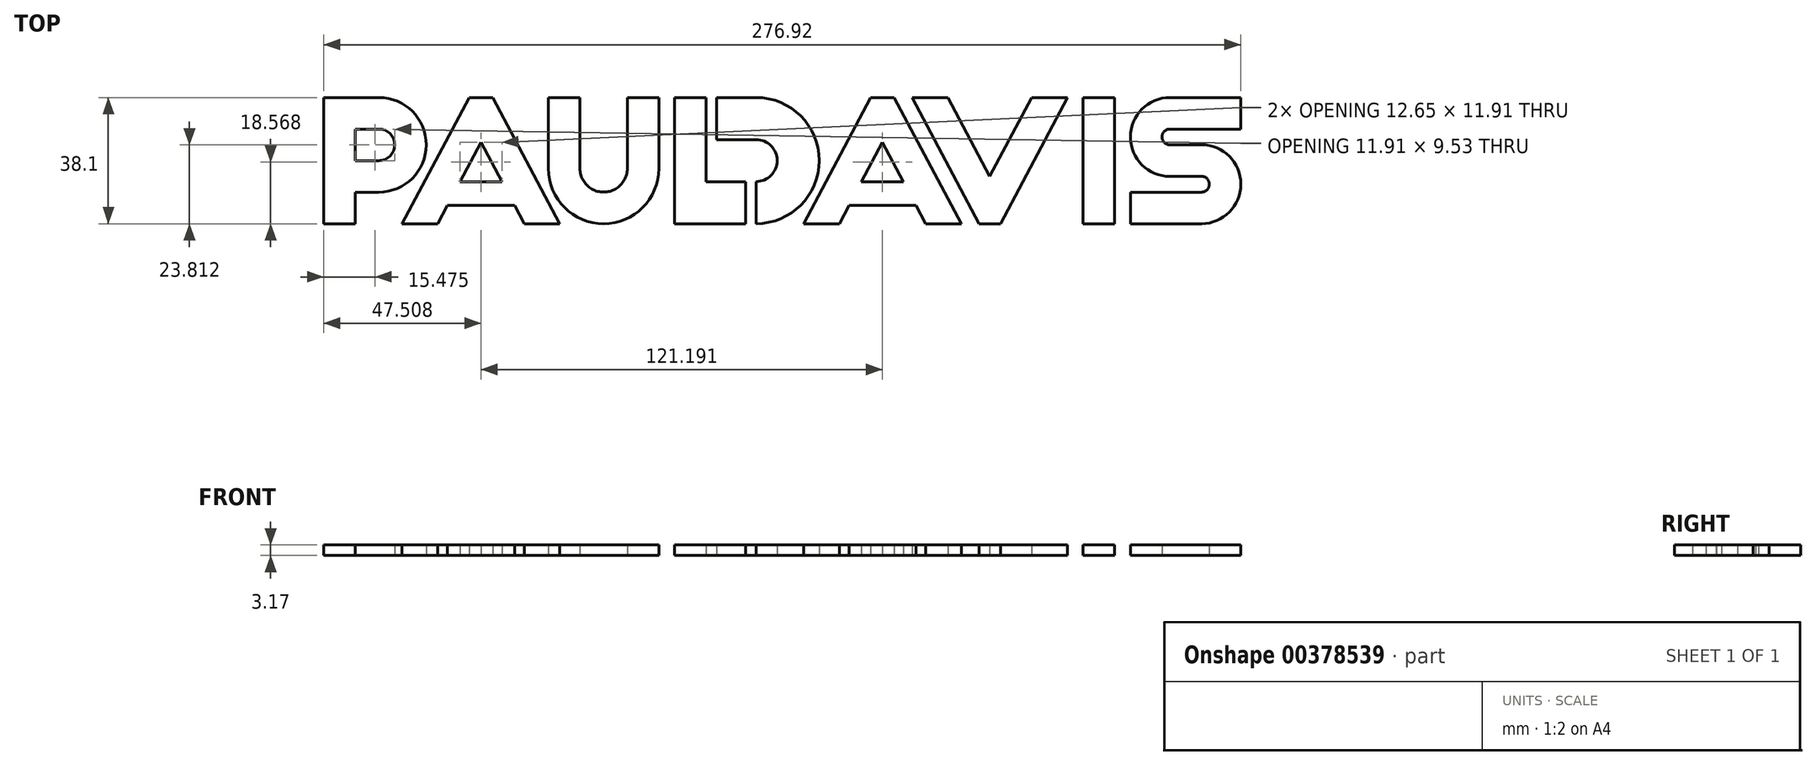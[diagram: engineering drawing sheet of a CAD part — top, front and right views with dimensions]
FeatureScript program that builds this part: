
annotation { "Feature Type Name" : "Feature", "Feature Type Description" : "" }
export const myFeature = defineFeature(function(context is Context, id is Id, definition is map)
    precondition{}
    {
        {
            var Q0;
            Q0=qCreatedBy(makeId("Top.planeOp"),FACE);
            var sketch = newSketch(context, id + "F0", { "sketchPlane" : qUnion([Q0])});
            skLineSegment(sketch, "E0.bottom", {"start": v(-32.5, 19.05) * mm, "end": v(-22.98, 19.05) * mm});
            skLineSegment(sketch, "E0.top", {"start": v(-32.5, -19.05) * mm, "end": v(-22.98, -19.05) * mm});
            skLineSegment(sketch, "E0.left", {"start": v(-32.5, 19.05) * mm, "end": v(-32.5, -19.05) * mm});
            skLineSegment(sketch, "E0.right", {"start": v(-22.98, 19.05) * mm, "end": v(-22.98, -6.35) * mm});
            skArc(sketch, "E1", {"start": v(-7.9, -19.05) * mm, "mid": v(11.15, 0) * mm, "end": v(-7.9, 19.05) * mm});
            skArc(sketch, "E2", {"start": v(-7.9, -6.35) * mm, "mid": v(-1.55, 0) * mm, "end": v(-7.9, 6.35) * mm});
            skLineSegment(sketch, "E3", {"start": v(-19.8, 19.05) * mm, "end": v(-7.9, 19.05) * mm});
            skLineSegment(sketch, "E4", {"start": v(-11.07, -19.05) * mm, "end": v(-22.98, -19.05) * mm});
            skLineSegment(sketch, "E5", {"start": v(-11.07, -6.35) * mm, "end": v(-22.98, -6.35) * mm});
            skLineSegment(sketch, "E6", {"start": v(-7.9, 6.35) * mm, "end": v(-19.8, 6.35) * mm});
            skLineSegment(sketch, "E7", {"start": v(-7.9, 19.05) * mm, "end": v(-7.9, -19.05) * mm, "construction": true});
            skLineSegment(sketch, "E8", {"start": v(-7.9, 0) * mm, "end": v(11.15, 0) * mm, "construction": true});
            skLineSegment(sketch, "E9", {"start": v(-19.8, 19.05) * mm, "end": v(-19.8, 6.35) * mm});
            skLineSegment(sketch, "E10", {"start": v(-7.9, 0) * mm, "end": v(-22.98, 0) * mm, "construction": true});
            skLineSegment(sketch, "E11", {"start": v(-11.07, -6.35) * mm, "end": v(-11.07, -19.05) * mm});
            skLineSegment(sketch, "E12", {"start": v(-7.9, -6.35) * mm, "end": v(-7.9, -19.05) * mm});
            skLineSegment(sketch, "E13", {"start": v(-32.5, -19.05) * mm, "end": v(11.15, -19.05) * mm, "construction": true});
            skLineSegment(sketch, "E14", {"start": v(11.15, -19.05) * mm, "end": v(11.15, 0) * mm, "construction": true});
            skLineSegment(sketch, "E15", {"start": v(-94.52, 19.05) * mm, "end": v(-87.38, 19.05) * mm});
            skLineSegment(sketch, "E16", {"start": v(-87.38, 19.05) * mm, "end": v(-67.14, -19.05) * mm});
            skLineSegment(sketch, "E17", {"start": v(-94.52, 19.05) * mm, "end": v(-114.76, -19.05) * mm});
            skArc(sketch, "E18", {"start": v(-70.6, -2.38) * mm, "mid": v(-53.93, -19.05) * mm, "end": v(-37.26, -2.38) * mm});
            skArc(sketch, "E19", {"start": v(-61.08, -2.38) * mm, "mid": v(-53.93, -9.52) * mm, "end": v(-46.79, -2.38) * mm});
            skLineSegment(sketch, "E20", {"start": v(-53.93, -19.05) * mm, "end": v(-53.93, -9.52) * mm, "construction": true});
            skLineSegment(sketch, "E21", {"start": v(-70.6, -2.38) * mm, "end": v(-61.08, -2.38) * mm, "construction": true});
            skLineSegment(sketch, "E22.trimOffspring", {"start": v(-46.79, -2.38) * mm, "end": v(-37.26, -2.38) * mm, "construction": true});
            skLineSegment(sketch, "E23", {"start": v(-70.6, -2.38) * mm, "end": v(-70.6, 19.05) * mm});
            skLineSegment(sketch, "E24", {"start": v(-70.6, 19.05) * mm, "end": v(-61.08, 19.05) * mm});
            skLineSegment(sketch, "E25", {"start": v(-61.08, 19.05) * mm, "end": v(-61.08, -2.38) * mm});
            skLineSegment(sketch, "E26", {"start": v(-46.79, -2.38) * mm, "end": v(-46.79, 19.05) * mm});
            skLineSegment(sketch, "E27", {"start": v(-46.79, 19.05) * mm, "end": v(-37.26, 19.05) * mm});
            skLineSegment(sketch, "E28", {"start": v(-37.26, 19.05) * mm, "end": v(-37.26, -2.38) * mm});
            skLineSegment(sketch, "E29", {"start": v(-37.26, -2.38) * mm, "end": v(-32.5, -2.38) * mm, "construction": true});
            skLineSegment(sketch, "E30", {"start": v(-101.07, -13.58) * mm, "end": v(-80.83, -13.58) * mm});
            skLineSegment(sketch, "E31", {"start": v(-97.28, -6.44) * mm, "end": v(-84.63, -6.44) * mm});
            skLineSegment(sketch, "E32", {"start": v(-90.95, 5.47) * mm, "end": v(-97.28, -6.44) * mm});
            skLineSegment(sketch, "E33", {"start": v(-77.93, -19.05) * mm, "end": v(-80.83, -13.58) * mm});
            skLineSegment(sketch, "E34", {"start": v(-114.76, -19.05) * mm, "end": v(-103.98, -19.05) * mm});
            skLineSegment(sketch, "E35", {"start": v(-67.14, -19.05) * mm, "end": v(-77.93, -19.05) * mm});
            skLineSegment(sketch, "E36", {"start": v(-114.76, -19.05) * mm, "end": v(-67.14, -19.05) * mm, "construction": true});
            skLineSegment(sketch, "E37.trimOffspring", {"start": v(-84.63, -6.44) * mm, "end": v(-90.95, 5.47) * mm});
            skLineSegment(sketch, "E38.trimOffspring", {"start": v(-101.07, -13.58) * mm, "end": v(-103.98, -19.05) * mm});
            skLineSegment(sketch, "E39", {"start": v(-70.6, -2.38) * mm, "end": v(-74.8, -4.62) * mm, "construction": true});
            skLineSegment(sketch, "E40", {"start": v(26.67, 19.05) * mm, "end": v(33.81, 19.05) * mm});
            skLineSegment(sketch, "E41", {"start": v(33.81, 19.05) * mm, "end": v(54.05, -19.05) * mm});
            skLineSegment(sketch, "E42", {"start": v(26.67, 19.05) * mm, "end": v(6.43, -19.05) * mm});
            skLineSegment(sketch, "E43", {"start": v(20.12, -13.58) * mm, "end": v(40.36, -13.58) * mm});
            skLineSegment(sketch, "E44", {"start": v(23.91, -6.44) * mm, "end": v(36.56, -6.44) * mm});
            skLineSegment(sketch, "E45", {"start": v(30.24, 5.47) * mm, "end": v(23.91, -6.44) * mm});
            skLineSegment(sketch, "E46", {"start": v(43.27, -19.05) * mm, "end": v(40.36, -13.58) * mm});
            skLineSegment(sketch, "E47", {"start": v(6.43, -19.05) * mm, "end": v(17.21, -19.05) * mm});
            skLineSegment(sketch, "E48", {"start": v(54.05, -19.05) * mm, "end": v(43.27, -19.05) * mm});
            skLineSegment(sketch, "E49", {"start": v(6.43, -19.05) * mm, "end": v(54.05, -19.05) * mm, "construction": true});
            skLineSegment(sketch, "E50.trimOffspring", {"start": v(36.56, -6.44) * mm, "end": v(30.24, 5.47) * mm});
            skLineSegment(sketch, "E51.trimOffspring", {"start": v(20.12, -13.58) * mm, "end": v(17.21, -19.05) * mm});
            skLineSegment(sketch, "E52", {"start": v(11.15, 0) * mm, "end": v(15.36, -2.23) * mm, "construction": true});
            skArc(sketch, "E53", {"start": v(-121.8, -9.53) * mm, "mid": v(-107.5, 4.76) * mm, "end": v(-121.8, 19.05) * mm});
            skArc(sketch, "E54", {"start": v(-121.8, 0) * mm, "mid": v(-117.03, 4.76) * mm, "end": v(-121.8, 9.52) * mm});
            skLineSegment(sketch, "E55", {"start": v(-121.8, 19.05) * mm, "end": v(-94.52, 19.05) * mm, "construction": true});
            skLineSegment(sketch, "E56", {"start": v(-107.5, 4.76) * mm, "end": v(-103.3, 2.53) * mm, "construction": true});
            skLineSegment(sketch, "E57", {"start": v(-121.8, 19.05) * mm, "end": v(-138.46, 19.05) * mm});
            skLineSegment(sketch, "E58", {"start": v(-121.8, 9.52) * mm, "end": v(-128.94, 9.52) * mm});
            skLineSegment(sketch, "E59", {"start": v(-121.8, 0) * mm, "end": v(-128.94, 0) * mm});
            skLineSegment(sketch, "E60", {"start": v(-121.8, -9.53) * mm, "end": v(-128.94, -9.53) * mm});
            skLineSegment(sketch, "E61", {"start": v(-138.46, 19.05) * mm, "end": v(-138.46, -19.05) * mm});
            skLineSegment(sketch, "E62", {"start": v(-138.46, -19.05) * mm, "end": v(-128.94, -19.05) * mm});
            skLineSegment(sketch, "E63", {"start": v(-128.94, -19.05) * mm, "end": v(-128.94, -9.53) * mm});
            skLineSegment(sketch, "E64", {"start": v(-128.94, 9.52) * mm, "end": v(-128.94, 0) * mm});
            skLineSegment(sketch, "E65", {"start": v(39.2, 19.05) * mm, "end": v(49.99, 19.05) * mm});
            skLineSegment(sketch, "E66", {"start": v(49.99, 19.05) * mm, "end": v(62.64, -4.76) * mm});
            skLineSegment(sketch, "E67", {"start": v(62.64, -4.76) * mm, "end": v(75.3, 19.05) * mm});
            skLineSegment(sketch, "E68", {"start": v(75.3, 19.05) * mm, "end": v(86.08, 19.05) * mm});
            skLineSegment(sketch, "E69", {"start": v(86.08, 19.05) * mm, "end": v(65.84, -19.05) * mm});
            skLineSegment(sketch, "E70", {"start": v(65.84, -19.05) * mm, "end": v(59.44, -19.05) * mm});
            skLineSegment(sketch, "E71", {"start": v(59.44, -19.05) * mm, "end": v(39.2, 19.05) * mm});
            skLineSegment(sketch, "E72", {"start": v(49.32, 0) * mm, "end": v(45.12, -2.23) * mm, "construction": true});
            skLineSegment(sketch, "E73.bottom", {"start": v(90.84, 19.05) * mm, "end": v(100.36, 19.05) * mm});
            skLineSegment(sketch, "E73.top", {"start": v(90.84, -19.05) * mm, "end": v(100.36, -19.05) * mm});
            skLineSegment(sketch, "E73.left", {"start": v(90.84, 19.05) * mm, "end": v(90.84, -19.05) * mm});
            skLineSegment(sketch, "E73.right", {"start": v(100.36, 19.05) * mm, "end": v(100.36, -19.05) * mm});
            skLineSegment(sketch, "E74", {"start": v(90.84, 19.05) * mm, "end": v(86.08, 19.05) * mm, "construction": true});
            skArc(sketch, "E75", {"start": v(126.56, -9.53) * mm, "mid": v(128.94, -7.14) * mm, "end": v(126.56, -4.76) * mm});
            skArc(sketch, "E76", {"start": v(126.56, -19.05) * mm, "mid": v(138.46, -7.14) * mm, "end": v(126.56, 4.76) * mm});
            skLineSegment(sketch, "E77", {"start": v(126.56, 4.76) * mm, "end": v(126.56, -19.05) * mm, "construction": true});
            skArc(sketch, "E78", {"start": v(117.03, 9.52) * mm, "mid": v(114.65, 7.14) * mm, "end": v(117.03, 4.76) * mm});
            skArc(sketch, "E79", {"start": v(117.03, 19.05) * mm, "mid": v(105.13, 7.14) * mm, "end": v(117.03, -4.76) * mm});
            skLineSegment(sketch, "E80", {"start": v(117.03, 19.05) * mm, "end": v(117.03, -4.76) * mm, "construction": true});
            skLineSegment(sketch, "E81", {"start": v(117.03, 4.76) * mm, "end": v(126.56, 4.76) * mm});
            skLineSegment(sketch, "E82", {"start": v(117.03, -4.76) * mm, "end": v(126.56, -4.76) * mm});
            skLineSegment(sketch, "E83", {"start": v(126.56, -19.05) * mm, "end": v(105.13, -19.05) * mm});
            skLineSegment(sketch, "E84", {"start": v(105.13, -19.05) * mm, "end": v(105.13, -9.53) * mm});
            skLineSegment(sketch, "E85", {"start": v(105.13, -9.53) * mm, "end": v(126.56, -9.53) * mm});
            skLineSegment(sketch, "E86", {"start": v(105.13, -9.53) * mm, "end": v(105.13, 7.14) * mm, "construction": true});
            skLineSegment(sketch, "E87", {"start": v(117.03, 19.05) * mm, "end": v(138.46, 19.05) * mm});
            skLineSegment(sketch, "E88", {"start": v(138.46, 19.05) * mm, "end": v(138.46, 9.52) * mm});
            skLineSegment(sketch, "E89", {"start": v(138.46, 9.52) * mm, "end": v(117.03, 9.52) * mm});
            skLineSegment(sketch, "E90", {"start": v(138.46, 9.52) * mm, "end": v(138.46, -7.14) * mm, "construction": true});
            skLineSegment(sketch, "E91", {"start": v(105.13, -1.2) * mm, "end": v(100.36, -1.2) * mm, "construction": true});
            skLineSegment(sketch, "E92", {"start": v(126.56, -19.05) * mm, "end": v(100.36, -19.05) * mm, "construction": true});
            skLineSegment(sketch, "E93", {"start": v(117.03, 19.05) * mm, "end": v(100.36, 19.05) * mm, "construction": true});
            skLineSegment(sketch, "E94.bottom", {"start": v(-138.46, 19.05) * mm, "end": v(138.46, 19.05) * mm, "construction": true});
            skLineSegment(sketch, "E94.top", {"start": v(-138.46, -19.05) * mm, "end": v(138.46, -19.05) * mm, "construction": true});
            skLineSegment(sketch, "E94.left", {"start": v(-138.46, 19.05) * mm, "end": v(-138.46, -19.05) * mm, "construction": true});
            skLineSegment(sketch, "E94.right", {"start": v(138.46, 19.05) * mm, "end": v(138.46, -19.05) * mm, "construction": true});
            skPoint(sketch, "E94.middle", {"position": v(0, 0) * mm});
            skLineSegment(sketch, "E95.bottom", {"start": v(-152.4, 76.2) * mm, "end": v(152.4, 76.2) * mm});
            skLineSegment(sketch, "E95.top", {"start": v(-152.4, -76.2) * mm, "end": v(152.4, -76.2) * mm});
            skLineSegment(sketch, "E95.left", {"start": v(-152.4, 76.2) * mm, "end": v(-152.4, -76.2) * mm});
            skLineSegment(sketch, "E95.right", {"start": v(152.4, 76.2) * mm, "end": v(152.4, -76.2) * mm});
            skLineSegment(sketch, "E96.bottom", {"start": v(-146.05, 69.85) * mm, "end": v(146.05, 69.85) * mm});
            skLineSegment(sketch, "E96.top", {"start": v(-146.05, -69.85) * mm, "end": v(146.05, -69.85) * mm});
            skLineSegment(sketch, "E96.left", {"start": v(-146.05, 69.85) * mm, "end": v(-146.05, -69.85) * mm});
            skLineSegment(sketch, "E96.right", {"start": v(146.05, 69.85) * mm, "end": v(146.05, -69.85) * mm});
            skSolve(sketch);
        }
        {
            var Q0;
            Q0=makeQuery(id+"F0.imprint","IMPRINT",FACE,{"disambiguationData":[TD([[makeQuery(id+"F0.imprint","IMPRINT",EDGE,{"derivedFrom":sQuery(id+"F0.wireOp",EDGE,"E53")}),1.0]])]});
            var Q1;
            Q1=makeQuery(id+"F0.imprint","IMPRINT",FACE,{"disambiguationData":[TD([[makeQuery(id+"F0.imprint","IMPRINT",EDGE,{"derivedFrom":sQuery(id+"F0.wireOp",EDGE,"E15")}),-1.0]])]});
            var Q2;
            Q2=makeQuery(id+"F0.imprint","IMPRINT",FACE,{"disambiguationData":[TD([[makeQuery(id+"F0.imprint","IMPRINT",EDGE,{"derivedFrom":sQuery(id+"F0.wireOp",EDGE,"E18")}),1.0]])]});
            var Q3;
            Q3=makeQuery(id+"F0.imprint","IMPRINT",FACE,{"disambiguationData":[TD([[makeQuery(id+"F0.imprint","IMPRINT",EDGE,{"derivedFrom":sQuery(id+"F0.wireOp",EDGE,"E0.bottom")}),-1.0]])]});
            var Q4;
            Q4=makeQuery(id+"F0.imprint","IMPRINT",FACE,{"disambiguationData":[TD([[makeQuery(id+"F0.imprint","IMPRINT",EDGE,{"derivedFrom":sQuery(id+"F0.wireOp",EDGE,"E1")}),1.0]])]});
            var Q5;
            Q5=makeQuery(id+"F0.imprint","IMPRINT",FACE,{"disambiguationData":[TD([[makeQuery(id+"F0.imprint","IMPRINT",EDGE,{"derivedFrom":sQuery(id+"F0.wireOp",EDGE,"E40")}),-1.0]])]});
            var Q6;
            Q6=makeQuery(id+"F0.imprint","IMPRINT",FACE,{"disambiguationData":[TD([[makeQuery(id+"F0.imprint","IMPRINT",EDGE,{"derivedFrom":sQuery(id+"F0.wireOp",EDGE,"E65")}),-1.0]])]});
            var Q7;
            Q7=makeQuery(id+"F0.imprint","IMPRINT",FACE,{"disambiguationData":[TD([[makeQuery(id+"F0.imprint","IMPRINT",EDGE,{"derivedFrom":sQuery(id+"F0.wireOp",EDGE,"E73.bottom")}),-1.0]])]});
            var Q8;
            Q8=makeQuery(id+"F0.imprint","IMPRINT",FACE,{"disambiguationData":[TD([[makeQuery(id+"F0.imprint","IMPRINT",EDGE,{"derivedFrom":sQuery(id+"F0.wireOp",EDGE,"E75")}),-1.0]])]});
            extrude(context, id + "F1", {"entities" : qUnion([Q0, Q1, Q2, Q3, Q4, Q5, Q6, Q7, Q8]), "depth" : 3.17 * mm, "offsetDistance" : 25.4 * mm});
        }
    });
